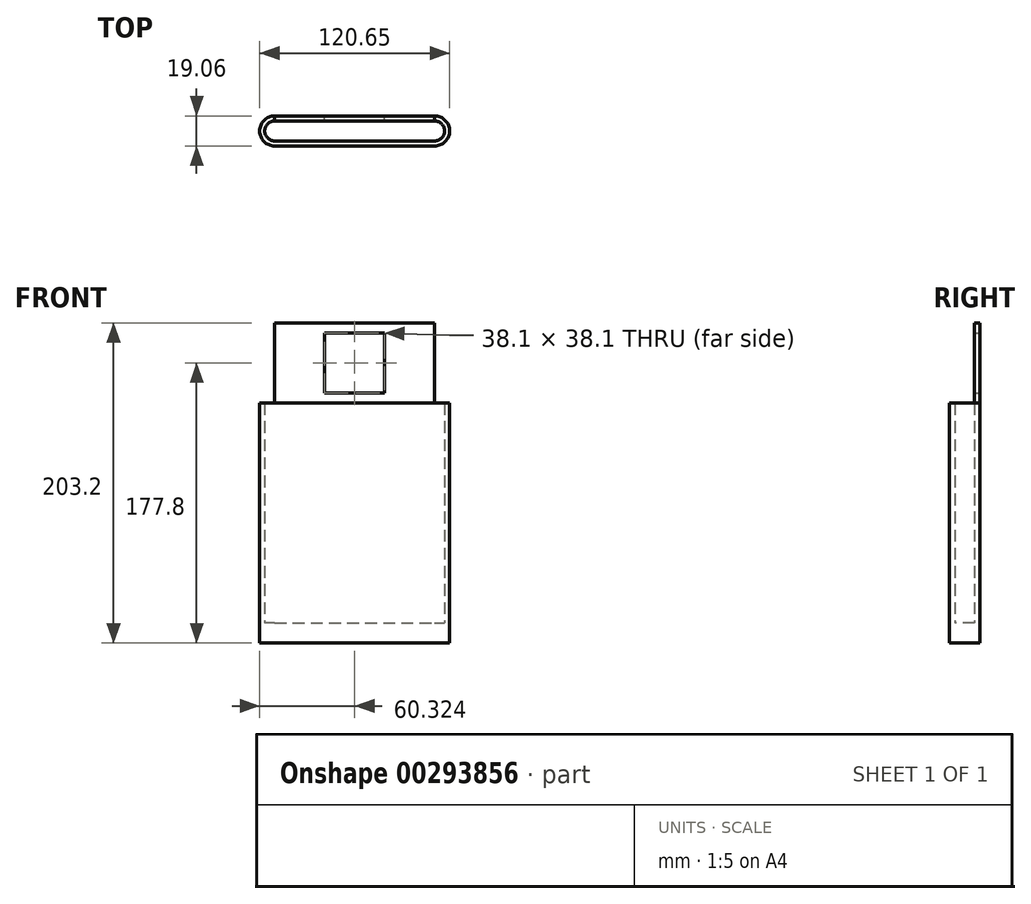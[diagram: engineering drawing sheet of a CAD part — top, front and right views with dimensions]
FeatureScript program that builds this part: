
annotation { "Feature Type Name" : "Feature", "Feature Type Description" : "" }
export const myFeature = defineFeature(function(context is Context, id is Id, definition is map)
    precondition{}
    {
        {
            var Q0;
            Q0=qCreatedBy(makeId("Top.planeOp"),FACE);
            var sketch = newSketch(context, id + "F0", { "sketchPlane" : qUnion([Q0])});
            skArc(sketch, "E0", {"start": v(-60.56, 6.35) * mm, "mid": v(-66.9, 0) * mm, "end": v(-60.56, -6.35) * mm});
            skArc(sketch, "E1", {"start": v(41.04, -6.35) * mm, "mid": v(47.4, 0) * mm, "end": v(41.04, 6.35) * mm});
            skLineSegment(sketch, "E2", {"start": v(-60.56, 6.35) * mm, "end": v(41.04, 6.35) * mm});
            skLineSegment(sketch, "E3", {"start": v(-60.56, -6.35) * mm, "end": v(41.04, -6.35) * mm});
            skArc(sketch, "E4", {"start": v(-60.56, 9.53) * mm, "mid": v(-70.08, 0) * mm, "end": v(-60.56, -9.53) * mm});
            skArc(sketch, "E5", {"start": v(41.04, -9.53) * mm, "mid": v(50.57, 0) * mm, "end": v(41.04, 9.53) * mm});
            skLineSegment(sketch, "E6", {"start": v(-60.56, 9.53) * mm, "end": v(41.04, 9.53) * mm});
            skLineSegment(sketch, "E7", {"start": v(41.04, -9.53) * mm, "end": v(-60.56, -9.53) * mm});
            skLineSegment(sketch, "E8", {"start": v(-60.56, -6.35) * mm, "end": v(-60.56, -9.53) * mm});
            skLineSegment(sketch, "E9", {"start": v(41.04, -6.35) * mm, "end": v(41.04, -9.53) * mm});
            skSolve(sketch);
        }
        {
            var Q0;
            Q0=makeQuery(id+"F0.imprint","IMPRINT",FACE,{"disambiguationData":[TD([[makeQuery(id+"F0.imprint","IMPRINT",EDGE,{"derivedFrom":sQuery(id+"F0.wireOp",EDGE,"E0")}),1.0]])]});
            extrude(context, id + "F1", {"entities" : qUnion([Q0]), "depth" : 12.7 * mm});
        }
        {
            var Q0;
            Q0 = qSketchRegion(id + "F0", true);
            extrude(context, id + "F2", {"entities" : qUnion([Q0]), "operationType" : NewBodyOperationType.ADD, "depth" : 152.4 * mm});
        }
        {
            var Q0;
            Q0=makeQuery(id+"F0.imprint","IMPRINT",FACE,{"disambiguationData":[TD([[makeQuery(id+"F0.imprint","IMPRINT",EDGE,{"derivedFrom":sQuery(id+"F0.wireOp",EDGE,"E3")}),-1.0]])]});
            extrude(context, id + "F3", {"entities" : qUnion([Q0]), "operationType" : NewBodyOperationType.ADD, "depth" : 50.8 * mm});
        }
        {
            var Q0;
            Q0=makeQuery(id+"F2.opExtrude","CAP_FACE",FACE,{"disambiguationData":[OSD([sQuery(id+"F0.wireOp",EDGE,"E0"),sQuery(id+"F0.wireOp",EDGE,"E1"),sQuery(id+"F0.wireOp",EDGE,"E2"),sQuery(id+"F0.wireOp",EDGE,"E3"),sQuery(id+"F0.wireOp",EDGE,"E4"),sQuery(id+"F0.wireOp",EDGE,"E5"),sQuery(id+"F0.wireOp",EDGE,"E6"),sQuery(id+"F0.wireOp",EDGE,"E7")])],"isStart":false});
            var sketch = newSketch(context, id + "F4", { "sketchPlane" : qUnion([Q0])});
            skLineSegment(sketch, "E10", {"start": v(-60.56, 6.35) * mm, "end": v(-60.56, 9.53) * mm});
            skLineSegment(sketch, "E11", {"start": v(41.04, 6.35) * mm, "end": v(41.04, 9.53) * mm});
            skSolve(sketch);
        }
        {
            var Q0;
            Q0=makeQuery(id+"F4.imprint","IMPRINT",FACE,{"disambiguationData":[TD([[makeQuery(id+"F4.imprint","IMPRINT",EDGE,{"derivedFrom":sQuery(id+"F4.wireOp",EDGE,"E10")}),-1.0]])]});
            extrude(context, id + "F5", {"entities" : qUnion([Q0]), "operationType" : NewBodyOperationType.ADD, "depth" : 50.8 * mm});
        }
        {
            var Q0;
            {var subQ0=sQuery(id+"F0.wireOp",EDGE,"E6");Q0=makeQuery(id+"F5.boolean.opBoolean","MERGE",FACE,{"derivedFrom":[makeQuery(id+"F2.opExtrude","SWEPT_FACE",FACE,{"disambiguationData":[OSD([subQ0])]}),makeQuery(id+"F5.opExtrude","SWEPT_FACE",FACE,{"disambiguationData":[OSD([subQ0])]})]});}
            var sketch = newSketch(context, id + "F6", { "sketchPlane" : qUnion([Q0])});
            skLineSegment(sketch, "E12.bottom", {"start": v(28.8, 158.75) * mm, "end": v(-9.3, 158.75) * mm});
            skLineSegment(sketch, "E12.top", {"start": v(28.8, 196.85) * mm, "end": v(-9.3, 196.85) * mm});
            skLineSegment(sketch, "E12.left", {"start": v(28.8, 158.75) * mm, "end": v(28.8, 196.85) * mm});
            skLineSegment(sketch, "E12.right", {"start": v(-9.3, 158.75) * mm, "end": v(-9.3, 196.85) * mm});
            skPoint(sketch, "E12.middle", {"position": v(9.76, 177.8) * mm});
            skPoint(sketch, "E12.middle.positionSnap0", {"position": v(9.76, 203.2) * mm});
            skPoint(sketch, "E12.centerSnap0", {"position": v(9.76, 203.2) * mm});
            skSolve(sketch);
        }
        {
            var Q0;
            Q0=makeQuery(id+"F6.imprint","IMPRINT",FACE,{"disambiguationData":[TD([[makeQuery(id+"F6.imprint","IMPRINT",EDGE,{"derivedFrom":sQuery(id+"F6.wireOp",EDGE,"E12.bottom")}),-1.0]])]});
            extrude(context, id + "F7", {"entities" : qUnion([Q0]), "operationType" : NewBodyOperationType.REMOVE, "oppositeDirection" : true, "depth" : 25.4 * mm});
        }
    });
